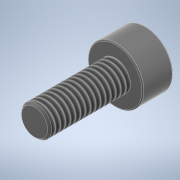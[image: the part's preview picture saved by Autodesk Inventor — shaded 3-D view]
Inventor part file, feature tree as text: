
AUTODESK INVENTOR PART (.ipt)
format: ipt  version: 2022 (Build 260153000, 153)  size: 146,944 bytes
history: native  units: in
note: dims shown in document units (in); Inventor stores cm internally (conversion verified against a paired STEP export)
features: sketch x3, extrude x2, plane x1, fillet x1, chamfer x1, thread x1
ambient origin geometry x8: Origin, YZ Plane, XZ Plane, XY Plane, X Axis, Y Axis, Z Axis, Center Point
bodies: Body1 (feature_tree)
feature tree (9):
  plane  "Work Plane1"
  fillet  "Fillet1"  [1 undecoded]
  extrude  "Extrusion2"  Depth=0.0039in
  extrude  "Extrusion1"  Depth=0.315in TaperAngle=0.0deg
  chamfer  "Chamfer1"  Distance=0.0079in
  thread  "Thread1"  [1 undecoded]
  sketch  "Sketch1"  dims[d1=0.1181in d2=0.0in d3=0.0039in]
  sketch  "Sketch2"  dims[d4=0.1181in d5=0.0in d6=0.315in d7=0.0in d8=0.0079in d9=0.0079in d10=17.7165in d11=0.3071in d12=0.0in]
  sketch  "Sketch3"
note: 2 required parameter values undecoded (feature->parameter linkage not recoverable at this tier; creation-order binding heuristic only, values carry confidence <= 0.55)
